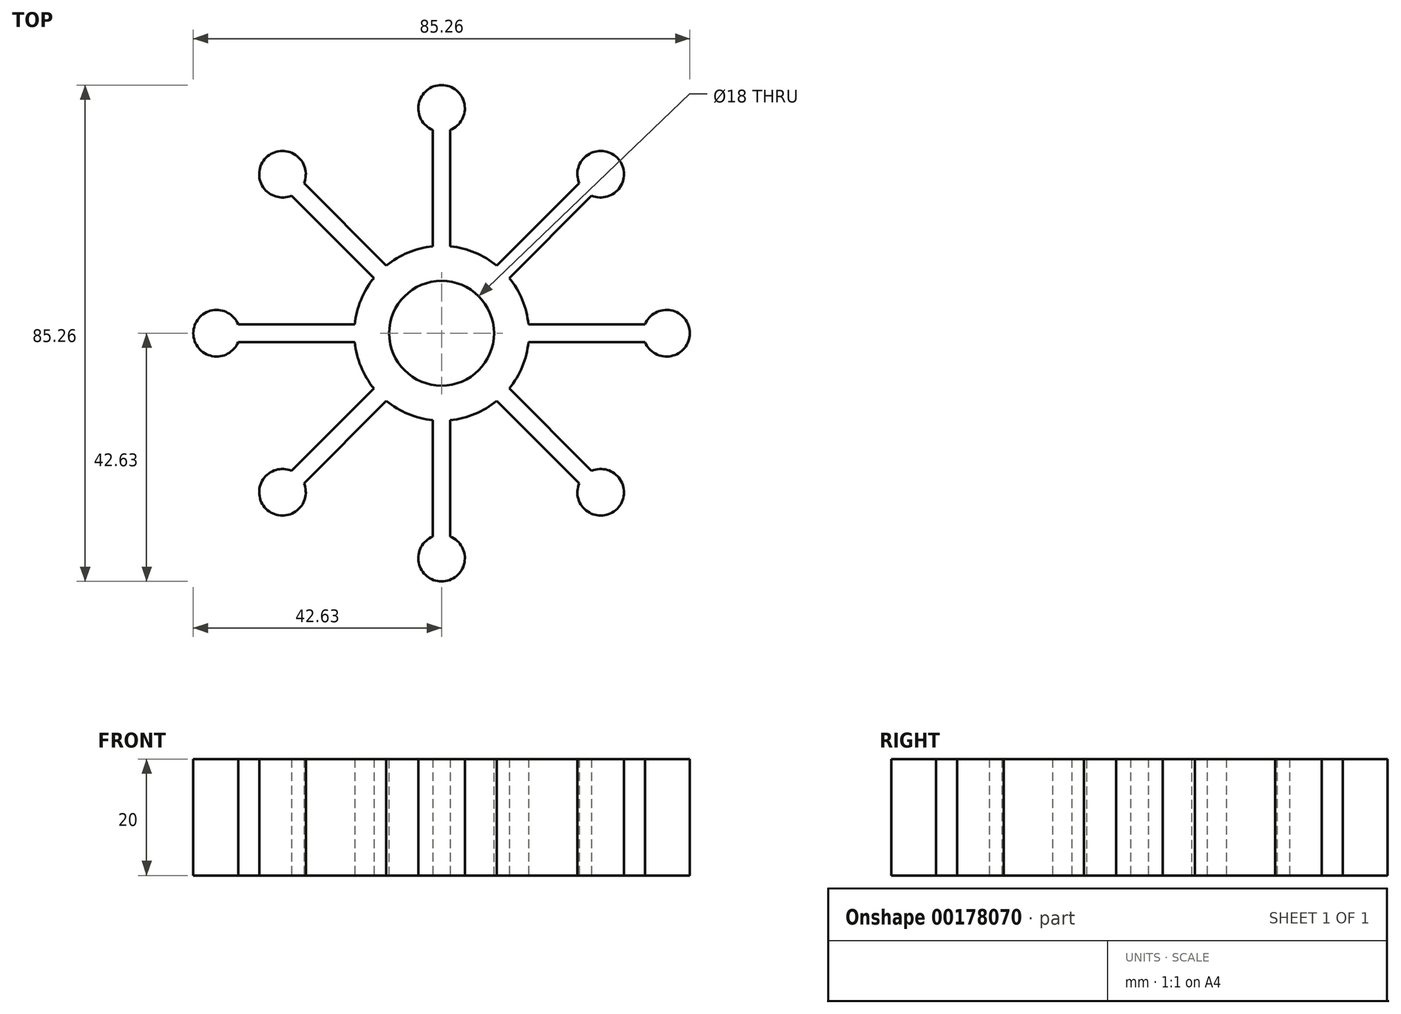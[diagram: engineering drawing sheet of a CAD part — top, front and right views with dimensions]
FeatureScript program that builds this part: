
annotation { "Feature Type Name" : "Feature", "Feature Type Description" : "" }
export const myFeature = defineFeature(function(context is Context, id is Id, definition is map)
    precondition{}
    {
        {
            var Q0;
            Q0=qCreatedBy(makeId("Top.planeOp"),FACE);
            var sketch = newSketch(context, id + "F0", { "sketchPlane" : qUnion([Q0])});
            skCircle(sketch, "E0", {"center": v(0, 0) * mm, "radius": 15 * mm});
            skLineSegment(sketch, "E1", {"start": v(0, 0) * mm, "end": v(0, 15) * mm, "construction": true});
            skCircle(sketch, "E2", {"center": v(0, 38.63) * mm, "radius": 4 * mm});
            skLineSegment(sketch, "E3", {"start": v(-1.5, 34.92) * mm, "end": v(-1.5, 14.92) * mm});
            skLineSegment(sketch, "E4.MirrorCS", {"start": v(1.5, 34.92) * mm, "end": v(1.5, 14.92) * mm});
            skCircle(sketch, "E5.1.0", {"center": v(-27.32, 27.32) * mm, "radius": 4 * mm});
            skLineSegment(sketch, "E5.1.1", {"start": v(-25.76, 23.63) * mm, "end": v(-11.61, 9.5) * mm});
            skLineSegment(sketch, "E5.1.2", {"start": v(-23.63, 25.76) * mm, "end": v(-9.5, 11.61) * mm});
            skCircle(sketch, "E5.2.0", {"center": v(-38.63, 0) * mm, "radius": 4 * mm});
            skLineSegment(sketch, "E5.2.1", {"start": v(-34.92, -1.5) * mm, "end": v(-14.92, -1.5) * mm});
            skLineSegment(sketch, "E5.2.2", {"start": v(-34.92, 1.5) * mm, "end": v(-14.92, 1.5) * mm});
            skCircle(sketch, "E6.1.3.0", {"center": v(-27.32, -27.32) * mm, "radius": 4 * mm});
            skLineSegment(sketch, "E6.2.3.0", {"start": v(-23.63, -25.76) * mm, "end": v(-9.5, -11.61) * mm});
            skLineSegment(sketch, "E6.5.3.0", {"start": v(-25.76, -23.63) * mm, "end": v(-11.61, -9.5) * mm});
            skCircle(sketch, "E6.1.4.0", {"center": v(0, -38.63) * mm, "radius": 4 * mm});
            skLineSegment(sketch, "E6.2.4.0", {"start": v(1.5, -34.92) * mm, "end": v(1.5, -14.92) * mm});
            skLineSegment(sketch, "E6.5.4.0", {"start": v(-1.5, -34.92) * mm, "end": v(-1.5, -14.92) * mm});
            skCircle(sketch, "E6.1.5.0", {"center": v(27.32, -27.32) * mm, "radius": 4 * mm});
            skLineSegment(sketch, "E6.2.5.0", {"start": v(25.76, -23.63) * mm, "end": v(11.61, -9.5) * mm});
            skLineSegment(sketch, "E6.5.5.0", {"start": v(23.63, -25.76) * mm, "end": v(9.5, -11.61) * mm});
            skCircle(sketch, "E6.1.6.0", {"center": v(38.63, 0) * mm, "radius": 4 * mm});
            skLineSegment(sketch, "E6.2.6.0", {"start": v(34.92, 1.5) * mm, "end": v(14.92, 1.5) * mm});
            skLineSegment(sketch, "E6.5.6.0", {"start": v(34.92, -1.5) * mm, "end": v(14.92, -1.5) * mm});
            skCircle(sketch, "E6.1.7.0", {"center": v(27.32, 27.32) * mm, "radius": 4 * mm});
            skLineSegment(sketch, "E6.2.7.0", {"start": v(23.63, 25.76) * mm, "end": v(9.5, 11.61) * mm});
            skLineSegment(sketch, "E6.5.7.0", {"start": v(25.76, 23.63) * mm, "end": v(11.61, 9.5) * mm});
            skSolve(sketch);
        }
        {
            var Q0;
            Q0=qSketchRegion(id+"F0",true);
            extrude(context, id + "F1", {"entities" : qUnion([Q0]), "depth" : 20 * mm});
        }
        {
            var Q0;
            Q0=makeQuery(id+"F1.opExtrude","CAP_FACE",FACE,{"disambiguationData":[OSD([sQuery(id+"F0.wireOp",EDGE,"E0"),sQuery(id+"F0.wireOp",EDGE,"E2"),sQuery(id+"F0.wireOp",EDGE,"E3"),sQuery(id+"F0.wireOp",EDGE,"E4.MirrorCS"),sQuery(id+"F0.wireOp",EDGE,"E5.1.0"),sQuery(id+"F0.wireOp",EDGE,"E5.1.1"),sQuery(id+"F0.wireOp",EDGE,"E5.1.2"),sQuery(id+"F0.wireOp",EDGE,"E5.2.0"),sQuery(id+"F0.wireOp",EDGE,"E5.2.1"),sQuery(id+"F0.wireOp",EDGE,"E5.2.2"),sQuery(id+"F0.wireOp",EDGE,"E6.1.3.0"),sQuery(id+"F0.wireOp",EDGE,"E6.2.3.0"),sQuery(id+"F0.wireOp",EDGE,"E6.5.3.0"),sQuery(id+"F0.wireOp",EDGE,"E6.1.4.0"),sQuery(id+"F0.wireOp",EDGE,"E6.2.4.0"),sQuery(id+"F0.wireOp",EDGE,"E6.5.4.0"),sQuery(id+"F0.wireOp",EDGE,"E6.1.5.0"),sQuery(id+"F0.wireOp",EDGE,"E6.2.5.0"),sQuery(id+"F0.wireOp",EDGE,"E6.5.5.0"),sQuery(id+"F0.wireOp",EDGE,"E6.1.6.0"),sQuery(id+"F0.wireOp",EDGE,"E6.2.6.0"),sQuery(id+"F0.wireOp",EDGE,"E6.5.6.0"),sQuery(id+"F0.wireOp",EDGE,"E6.1.7.0"),sQuery(id+"F0.wireOp",EDGE,"E6.2.7.0"),sQuery(id+"F0.wireOp",EDGE,"E6.5.7.0"),sQuery(id+"F0.wireOp",EDGE,"E6.1.8.0"),sQuery(id+"F0.wireOp",EDGE,"E6.2.8.0"),sQuery(id+"F0.wireOp",EDGE,"E6.5.8.0"),sQuery(id+"F0.wireOp",EDGE,"E6.1.9.0"),sQuery(id+"F0.wireOp",EDGE,"E6.2.9.0"),sQuery(id+"F0.wireOp",EDGE,"E6.5.9.0")])],"isStart":false});
            var sketch = newSketch(context, id + "F2", { "sketchPlane" : qUnion([Q0])});
            skCircle(sketch, "E7", {"center": v(0, 0) * mm, "radius": 9 * mm});
            skSolve(sketch);
        }
        {
            var Q0;
            Q0=qSketchRegion(id+"F2",true);
            extrude(context, id + "F3", {"entities" : qUnion([Q0]), "operationType" : NewBodyOperationType.REMOVE, "endBound" : BoundingType.THROUGH_ALL, "oppositeDirection" : true, "depth" : 25 * mm});
        }
    });
